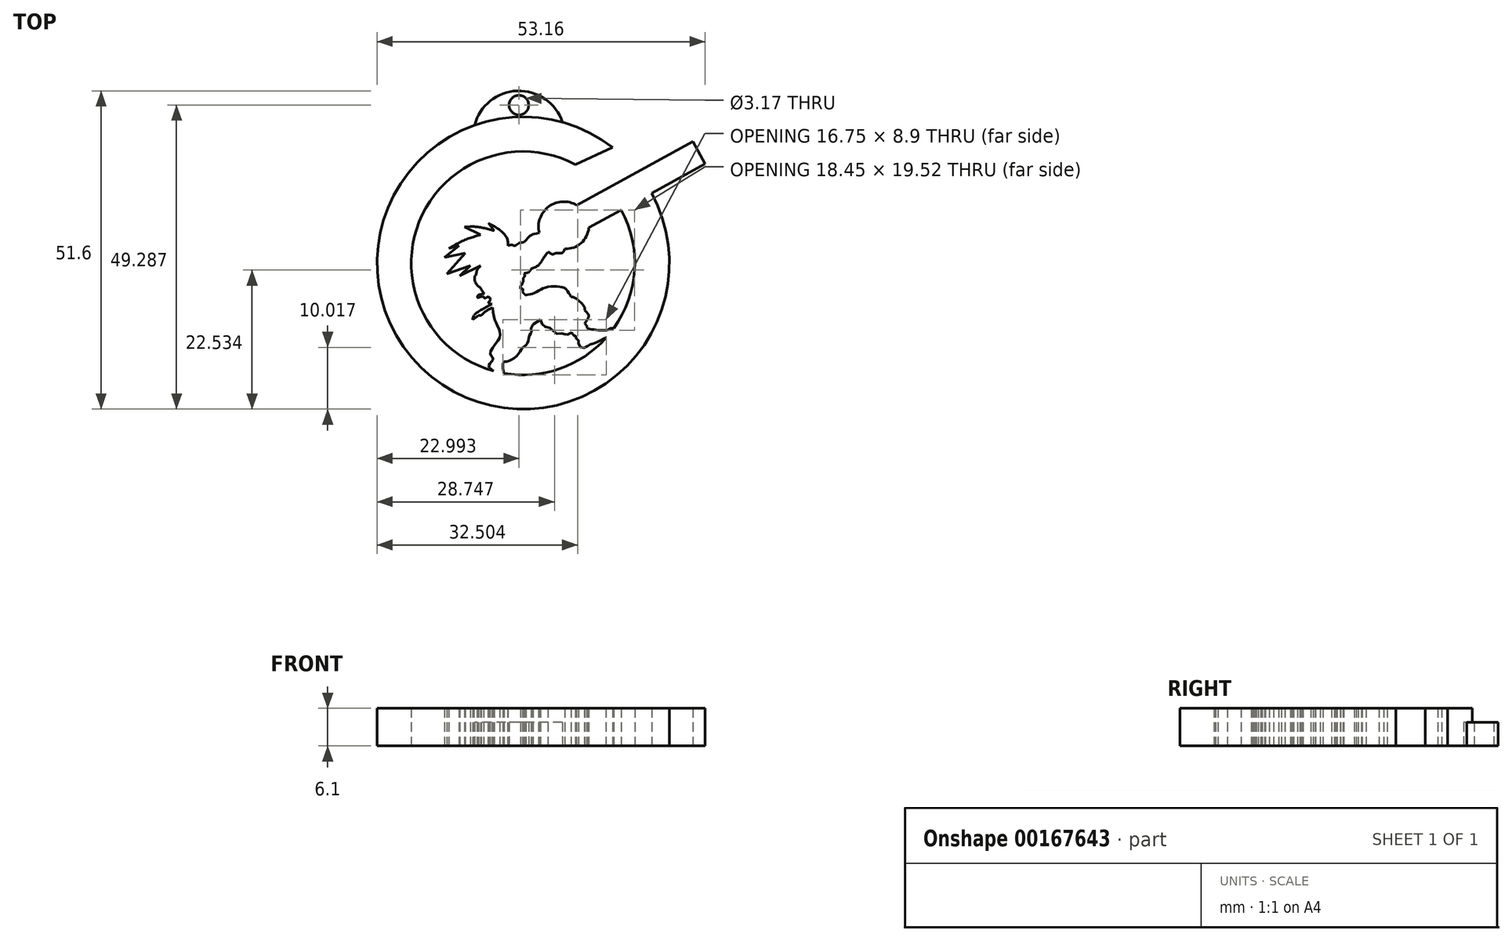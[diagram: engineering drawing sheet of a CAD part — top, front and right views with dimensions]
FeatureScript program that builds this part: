
annotation { "Feature Type Name" : "Feature", "Feature Type Description" : "" }
export const myFeature = defineFeature(function(context is Context, id is Id, definition is map)
    precondition{}
    {
        {
            var Q0;
            Q0=qCreatedBy(makeId("Top.planeOp"),FACE);
            var sketch = newSketch(context, id + "F0", { "sketchPlane" : qUnion([Q0])});
            skArc(sketch, "E0", {"start": v(11.9, 13.9) * mm, "mid": v(-20.63, -20.2) * mm, "end": v(18.22, 6.48) * mm});
            skPoint(sketch, "E0.first.point", {"position": v(-17.06, 13.92) * mm});
            skPoint(sketch, "E0.second.point", {"position": v(-12.4, -26.4) * mm});
            skPoint(sketch, "E0.third.point", {"position": v(21.03, -3.05) * mm});
            skArc(sketch, "E1", {"start": v(5.89, 11.12) * mm, "mid": v(-19.46, 1.82) * mm, "end": v(-7.4, -22.33) * mm});
            skPoint(sketch, "E1.first.point", {"position": v(-1.46, 13.21) * mm});
            skPoint(sketch, "E1.second.point", {"position": v(-16.81, -16.12) * mm});
            skPoint(sketch, "E1.third.point", {"position": v(15.37, -6.88) * mm});
            skLineSegment(sketch, "E2", {"start": v(5.89, 11.12) * mm, "end": v(11.9, 13.9) * mm});
            skLineSegment(sketch, "E3", {"start": v(6.07, 4.54) * mm, "end": v(24.89, 14.87) * mm});
            skLineSegment(sketch, "E4", {"start": v(24.89, 14.87) * mm, "end": v(26.88, 11.24) * mm});
            skLineSegment(sketch, "E5", {"start": v(26.88, 11.24) * mm, "end": v(18.22, 6.48) * mm});
            skArc(sketch, "E6", {"start": v(6.07, 4.54) * mm, "mid": v(1.55, 4.32) * mm, "end": v(0, 0.07) * mm});
            skArc(sketch, "E7", {"start": v(4.16, -2.54) * mm, "mid": v(6.79, -1.6) * mm, "end": v(8.04, 0.9) * mm});
            skLineSegment(sketch, "E8.trimOffspring", {"start": v(13.3, 3.78) * mm, "end": v(8.04, 0.9) * mm});
            skFitSpline(sketch, "E9", {"points": [v(-7.4, -22.33) * mm, v(-8.16, -21.42) * mm, v(-7.49, -20.4) * mm, v(-7.94, -19.45) * mm, v(-6.4, -16.86) * mm, v(-6.77, -15.03) * mm, v(-7.53, -12.05) * mm], "startDerivative": vector(-10.3, 6.52) * mm, "endDerivative": vector(-0.03, 19.25) * mm});
            skFitSpline(sketch, "E10", {"points": [v(-7.53, -12.05) * mm, v(-8.74, -12.7) * mm, v(-9.36, -13.3) * mm], "startDerivative": vector(-2.4, -1.12) * mm, "endDerivative": vector(-1.24, -1.4) * mm});
            skLineSegment(sketch, "E11", {"start": v(-9.36, -13.3) * mm, "end": v(-9.84, -13.3) * mm});
            skLineSegment(sketch, "E12", {"start": v(-9.84, -13.3) * mm, "end": v(-10.77, -14.01) * mm});
            skFitSpline(sketch, "E13", {"points": [v(-10.77, -14.01) * mm, v(-10.54, -13.3) * mm, v(-7.7, -11.5) * mm], "startDerivative": vector(0.19, 2.16) * mm, "endDerivative": vector(5.36, 2.78) * mm});
            skFitSpline(sketch, "E14", {"points": [v(-7.7, -11.5) * mm, v(-8.24, -11.24) * mm, v(-7.97, -10.93) * mm, v(-8.2, -10.3) * mm, v(-8.84, -10.55) * mm, v(-9.13, -10.28) * mm, v(-9.99, -10.45) * mm, v(-9.8, -9.97) * mm, v(-8.96, -9.78) * mm, v(-9.48, -8.88) * mm, v(-8.17, -8.59) * mm], "startDerivative": vector(-9, 2.85) * mm, "endDerivative": vector(14.35, 0.63) * mm});
            skFitSpline(sketch, "E15", {"points": [v(-9.48, -8.88) * mm, v(-10.15, -8.28) * mm, v(-10.49, -7.23) * mm, v(-10.22, -6.58) * mm, v(-10.1, -6) * mm, v(-9.48, -5.3) * mm], "startDerivative": vector(-3.44, 2.37) * mm, "endDerivative": vector(3.67, 3.33) * mm});
            skLineSegment(sketch, "E16", {"start": v(-9.48, -5.3) * mm, "end": v(-12.88, -6.9) * mm});
            skLineSegment(sketch, "E17", {"start": v(-12.88, -6.9) * mm, "end": v(-11.16, -5.3) * mm});
            skLineSegment(sketch, "E18", {"start": v(-11.16, -5.3) * mm, "end": v(-14.98, -6.6) * mm});
            skLineSegment(sketch, "E19", {"start": v(-14.98, -6.6) * mm, "end": v(-12, -3.21) * mm});
            skLineSegment(sketch, "E20", {"start": v(-12, -3.21) * mm, "end": v(-15.34, -3.9) * mm});
            skLineSegment(sketch, "E21", {"start": v(-15.34, -3.9) * mm, "end": v(-13, -2.04) * mm});
            skLineSegment(sketch, "E22", {"start": v(-13, -2.04) * mm, "end": v(-14.62, -2.47) * mm});
            skLineSegment(sketch, "E23", {"start": v(-9.48, -0.25) * mm, "end": v(-12.09, 1.02) * mm});
            skFitSpline(sketch, "E24", {"points": [v(-14.62, -2.47) * mm, v(-12.14, -1.13) * mm, v(-9.48, -0.25) * mm], "startDerivative": vector(4.87, 2.9) * mm, "endDerivative": vector(5.4, 1.55) * mm});
            skFitSpline(sketch, "E25", {"points": [v(-12.09, 1.02) * mm, v(-9.99, 1.02) * mm, v(-7.29, 0.4) * mm], "startDerivative": vector(4.4, 0.27) * mm, "endDerivative": vector(5.2, -1.47) * mm});
            skLineSegment(sketch, "E26", {"start": v(-7.29, 0.4) * mm, "end": v(-8.27, 1.64) * mm});
            skFitSpline(sketch, "E27", {"points": [v(-8.27, 1.64) * mm, v(-5.95, 0.16) * mm, v(-5.14, -1.09) * mm, v(-5.06, -2.03) * mm], "startDerivative": vector(6.1, -3.32) * mm, "endDerivative": vector(-0.37, -3.91) * mm});
            skFitSpline(sketch, "E28", {"points": [v(-5.06, -2.03) * mm, v(-4.52, -1.87) * mm, v(-3.92, -2.03) * mm, v(-3.32, -1.64) * mm, v(-2.45, -1.4) * mm, v(-1.48, -0.42) * mm, v(0, 0.07) * mm], "startDerivative": vector(5.77, 0.53) * mm, "endDerivative": vector(11.4, 3.47) * mm});
            skFitSpline(sketch, "E29", {"points": [v(4.16, -2.54) * mm, v(3.63, -3.24) * mm, v(2.8, -3.21) * mm, v(2.27, -3.4) * mm, v(1.43, -3.02) * mm], "startDerivative": vector(-1.58, -3.5) * mm, "endDerivative": vector(-3.35, 2.23) * mm});
            skFitSpline(sketch, "E30", {"points": [v(1.43, -3.02) * mm, v(0.62, -4.14) * mm, v(-0.1, -5.15) * mm, v(-1.31, -5.8) * mm], "startDerivative": vector(-2.52, -3.27) * mm, "endDerivative": vector(-3.97, -1.58) * mm});
            skFitSpline(sketch, "E31", {"points": [v(-1.31, -5.8) * mm, v(-1.72, -6.32) * mm, v(-2.46, -6.5) * mm], "startDerivative": vector(-0.7, -1.26) * mm, "endDerivative": vector(-1.58, -0.18) * mm});
            skFitSpline(sketch, "E32", {"points": [v(-2.46, -6.5) * mm, v(-2.36, -6.92) * mm, v(-2.6, -7.3) * mm], "startDerivative": vector(0.37, -0.86) * mm, "endDerivative": vector(-0.65, -0.74) * mm});
            skFitSpline(sketch, "E33", {"points": [v(-2.6, -7.3) * mm, v(-2.6, -7.76) * mm, v(-2.87, -8.42) * mm, v(-3, -8.54) * mm], "startDerivative": vector(0.15, -1.19) * mm, "endDerivative": vector(-0.57, -0.38) * mm});
            skLineSegment(sketch, "E34", {"start": v(-3, -8.54) * mm, "end": v(-3, -9.02) * mm});
            skFitSpline(sketch, "E35", {"points": [v(-3, -9.02) * mm, v(-2.69, -9.02) * mm, v(-2.7, -9.48) * mm], "startDerivative": vector(0.85, 0.19) * mm, "endDerivative": vector(-0.2, -1.06) * mm});
            skFitSpline(sketch, "E36", {"points": [v(-2.7, -9.48) * mm, v(-2.15, -10.05) * mm], "startDerivative": vector(0.38, -0.75) * mm, "endDerivative": vector(0.78, -0.51) * mm});
            skFitSpline(sketch, "E37", {"points": [v(-2.15, -10.05) * mm, v(-1, -9.77) * mm, v(0.22, -9.15) * mm, v(1.92, -8.63) * mm, v(3.74, -8.76) * mm, v(4.35, -9.11) * mm, v(4.94, -9.9) * mm, v(5.19, -10.32) * mm], "startDerivative": vector(8.03, 1.44) * mm, "endDerivative": vector(2.15, -4.13) * mm});
            skFitSpline(sketch, "E38", {"points": [v(5.19, -10.32) * mm, v(5.71, -10.43) * mm, v(6.79, -11.3) * mm, v(7.35, -12.07) * mm, v(7.34, -12.47) * mm], "startDerivative": vector(2.35, -0.09) * mm, "endDerivative": vector(-0.42, -2.15) * mm});
            skFitSpline(sketch, "E39", {"points": [v(7.34, -12.47) * mm, v(7.97, -13.18) * mm, v(8, -13.59) * mm, v(7.35, -14.64) * mm], "startDerivative": vector(2.16, -2.1) * mm, "endDerivative": vector(-2.07, -2.86) * mm});
            skLineSegment(sketch, "E40", {"start": v(7.35, -14.64) * mm, "end": v(7.84, -15.2) * mm});
            skFitSpline(sketch, "E41", {"points": [v(7.84, -15.2) * mm, v(7.75, -15.29) * mm, v(8.4, -15.57) * mm, v(11.22, -15.66) * mm, v(11.38, -15.49) * mm, v(12.1, -15.4) * mm], "startDerivative": vector(-1.63, -1.05) * mm, "endDerivative": vector(4.5, 0.05) * mm});
            skFitSpline(sketch, "E42", {"points": [v(-5.73, -22.7) * mm, v(-5.9, -21.42) * mm, v(-5.72, -20.8) * mm], "startDerivative": vector(-0.53, 2.37) * mm, "endDerivative": vector(0.6, 1.36) * mm});
            skFitSpline(sketch, "E43", {"points": [v(-5.72, -20.8) * mm, v(-5.16, -20.8) * mm, v(-3.62, -19.9) * mm, v(-2.71, -18.58) * mm, v(-2, -17.97) * mm, v(-1.48, -16.35) * mm, v(-1.22, -15.93) * mm, v(-1.3, -15.62) * mm, v(-1.02, -14.81) * mm], "startDerivative": vector(5.01, -0.8) * mm, "endDerivative": vector(3.9, 7.61) * mm});
            skLineSegment(sketch, "E44", {"start": v(-1.02, -14.81) * mm, "end": v(0.18, -14.05) * mm});
            skFitSpline(sketch, "E45", {"points": [v(0.18, -14.05) * mm, v(0.74, -15.03) * mm, v(1.88, -15.44) * mm, v(2.88, -16.32) * mm, v(3.95, -16.27) * mm, v(4.38, -16.52) * mm, v(5.21, -16.15) * mm, v(5.74, -16.72) * mm, v(5.86, -16.63) * mm, v(6.12, -17.2) * mm, v(6.37, -17.4) * mm, v(6.41, -18) * mm, v(6.93, -18.62) * mm, v(7.88, -18.27) * mm, v(8.32, -18) * mm, v(8.97, -17.85) * mm, v(9.83, -17.42) * mm, v(10.3, -17.19) * mm, v(10.84, -16.97) * mm], "startDerivative": vector(5.69, -17.11) * mm, "endDerivative": vector(11.24, 4.65) * mm});
            skArc(sketch, "E46.trimOffspring", {"start": v(-5.73, -22.7) * mm, "mid": v(3.3, -21.98) * mm, "end": v(10.84, -16.97) * mm});
            skArc(sketch, "E47.trimOffspring", {"start": v(12.1, -15.4) * mm, "mid": v(15.45, -5.99) * mm, "end": v(13.3, 3.78) * mm});
            skArc(sketch, "E48", {"start": v(3.76, 17.98) * mm, "mid": v(-3.54, 23.08) * mm, "end": v(-10.48, 17.5) * mm});
            skCircle(sketch, "E49", {"center": v(-3.29, 20.77) * mm, "radius": 1.59 * mm});
            skSolve(sketch);
        }
        {
            var Q0;
            Q0=makeQuery(id+"F0.imprint","IMPRINT",FACE,{"disambiguationData":[TD([[makeQuery(id+"F0.imprint","IMPRINT",EDGE,{"derivedFrom":sQuery(id+"F0.wireOp",EDGE,"E0")}),1.0]])]});
            extrude(context, id + "F1", {"entities" : qUnion([Q0]), "depth" : 6.1 * mm});
        }
        {
            var Q0;
            {var subQ0=sQuery(id+"F0.wireOp",EDGE,"E48");Q0=makeQuery(id+"F0.imprint","IMPRINT",FACE,{"disambiguationData":[TD([[makeQuery(id+"F0.imprint","IMPRINT",EDGE,{"derivedFrom":subQ0}),1.0]])]});}
            extrude(context, id + "F2", {"entities" : qUnion([Q0]), "operationType" : NewBodyOperationType.ADD, "depth" : 3.8 * mm});
        }
    });
